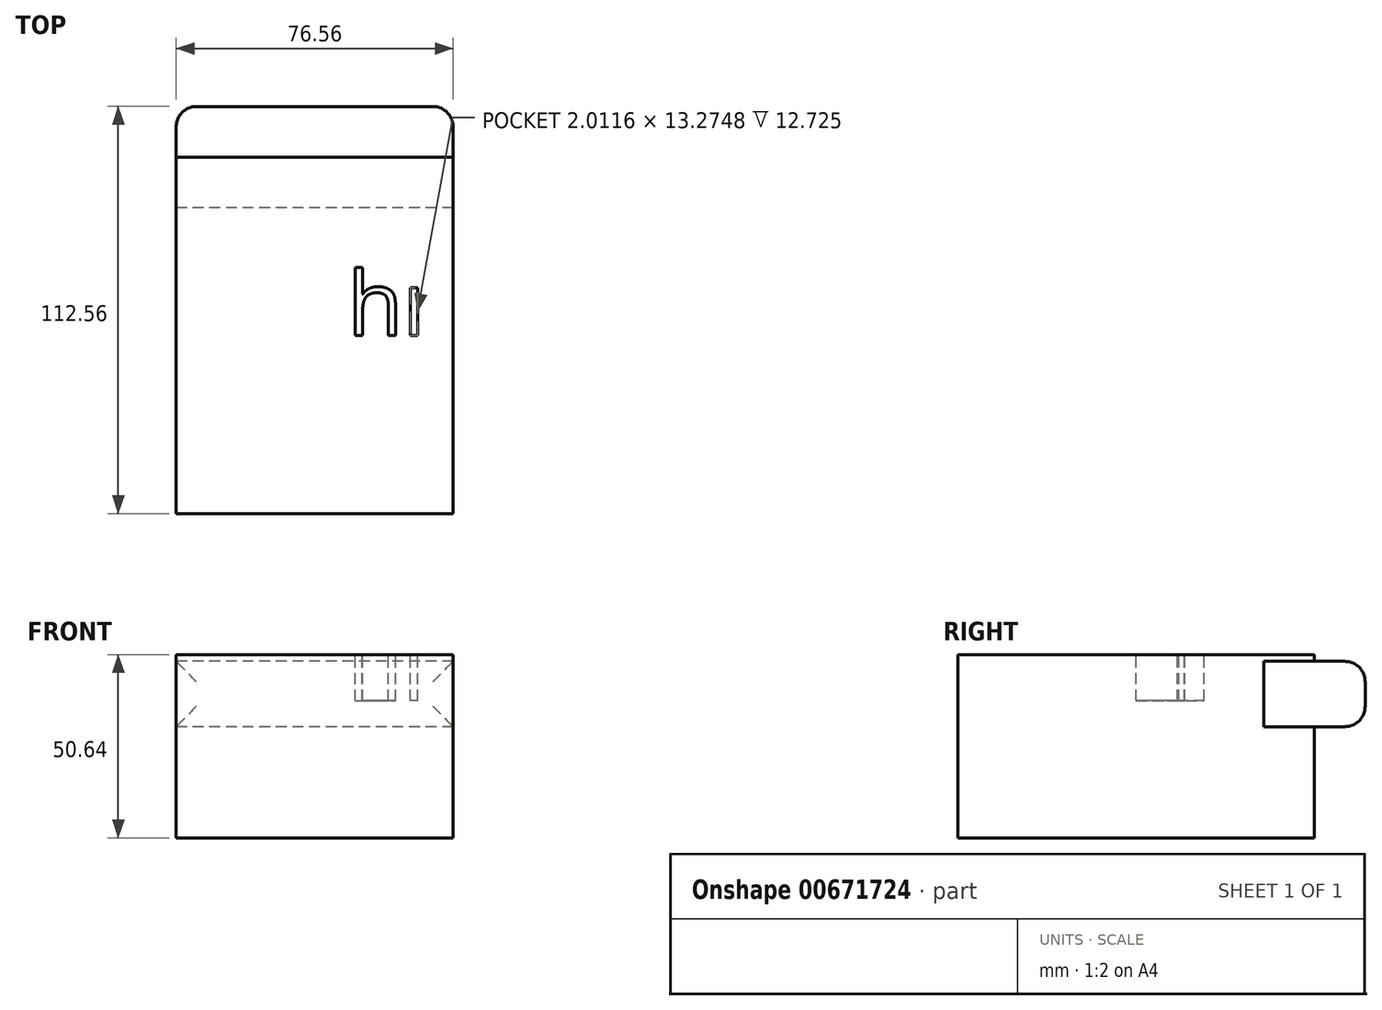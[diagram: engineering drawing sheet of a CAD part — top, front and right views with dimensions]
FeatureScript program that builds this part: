
annotation { "Feature Type Name" : "Feature", "Feature Type Description" : "" }
export const myFeature = defineFeature(function(context is Context, id is Id, definition is map)
    precondition{}
    {
        {
            var Q0;
            Q0=qCreatedBy(makeId("Right.planeOp"),FACE);
            var sketch = newSketch(context, id + "F0", { "sketchPlane" : qUnion([Q0])});
            skLineSegment(sketch, "E0.bottom", {"start": v(70.99, 0) * mm, "end": v(-27.58, 0) * mm});
            skLineSegment(sketch, "E0.top", {"start": v(70.99, 50.64) * mm, "end": v(-27.58, 50.64) * mm});
            skLineSegment(sketch, "E0.left", {"start": v(70.99, 0) * mm, "end": v(70.99, 50.64) * mm});
            skLineSegment(sketch, "E0.right", {"start": v(-27.58, 0) * mm, "end": v(-27.58, 50.64) * mm});
            skPoint(sketch, "E0.middle", {"position": v(21.7, 25.32) * mm});
            skLineSegment(sketch, "E1.bottom", {"start": v(84.98, 48.8) * mm, "end": v(57, 48.8) * mm});
            skLineSegment(sketch, "E1.top", {"start": v(84.98, 30.74) * mm, "end": v(57, 30.74) * mm});
            skLineSegment(sketch, "E1.left", {"start": v(84.98, 48.8) * mm, "end": v(84.98, 30.74) * mm});
            skLineSegment(sketch, "E1.right", {"start": v(57, 48.8) * mm, "end": v(57, 30.74) * mm});
            skPoint(sketch, "E1.middle", {"position": v(70.99, 39.77) * mm});
            skSolve(sketch);
        }
        {
            var Q0;
            {var subQ4=sQuery(id+"F0.wireOp",EDGE,"E0.bottom");Q0=makeQuery(id+"F0.imprint","IMPRINT",FACE,{"disambiguationData":[TD([[makeQuery(id+"F0.imprint","IMPRINT",EDGE,{"derivedFrom":subQ4}),-1.0]])]});}
            var sketch = newSketch(context, id + "F1", { "sketchPlane" : qUnion([Q0])});
            skSolve(sketch);
        }
        {
            var Q0;
            {var subQ4=sQuery(id+"F0.wireOp",EDGE,"E0.bottom");Q0=makeQuery(id+"F1.imprint","IMPRINT",FACE,{"disambiguationData":[TD([[makeQuery(id+"F1.imprint","IMPRINT",EDGE,{"derivedFrom":makeQuery(id+"F0.imprint","IMPRINT",EDGE,{"derivedFrom":subQ4})}),-1.0]])]});}
            var Q1;
            {var subQ5=sQuery(id+"F0.wireOp",EDGE,"E1.left");Q1=makeQuery(id+"F0.imprint","IMPRINT",FACE,{"disambiguationData":[TD([[makeQuery(id+"F0.imprint","IMPRINT",EDGE,{"derivedFrom":subQ5}),-1.0]])]});}
            var Q2;
            {var subQ5=sQuery(id+"F0.wireOp",EDGE,"E1.right");Q2=makeQuery(id+"F0.imprint","IMPRINT",FACE,{"disambiguationData":[TD([[makeQuery(id+"F0.imprint","IMPRINT",EDGE,{"derivedFrom":subQ5}),1.0]])]});}
            extrude(context, id + "F2", {"entities" : qUnion([Q0, Q1, Q2]), "depth" : 76.56 * mm, "offsetDistance" : 25.4 * mm});
        }
        {
            var Q0;
            Q0=makeQuery(id+"F2.opExtrude","SWEPT_EDGE",EDGE,{"disambiguationData":[OSD([sQuery(id+"F0.wireOp",EDGE,"E1.top"),sQuery(id+"F0.wireOp",EDGE,"E1.left")])]});
            var Q1;
            Q1=makeQuery(id+"F2.opExtrude","SWEPT_EDGE",EDGE,{"disambiguationData":[OSD([sQuery(id+"F0.wireOp",EDGE,"E1.bottom"),sQuery(id+"F0.wireOp",EDGE,"E1.left")])]});
            var Q2;
            Q2=makeQuery(id+"F2.opExtrude","CAP_EDGE",EDGE,{"disambiguationData":[OSD([sQuery(id+"F0.wireOp",EDGE,"E1.left")])],"isStart":false});
            var Q3;
            Q3=makeQuery(id+"F2.opExtrude","CAP_EDGE",EDGE,{"disambiguationData":[OSD([sQuery(id+"F0.wireOp",EDGE,"E1.left")])],"isStart":true});
            fillet(context, id + "F3", {"entities" : qUnion([Q0, Q1, Q2, Q3]), "radius" : 5.6 * mm, "tangentPropagation" : true, "allowEdgeOverflow" : false});
        }
        {
            var Q0;
            Q0=makeQuery(id+"F2.opExtrude","SWEPT_FACE",FACE,{"disambiguationData":[OSD([sQuery(id+"F0.wireOp",EDGE,"E0.top")])]});
            var sketch = newSketch(context, id + "F4", { "sketchPlane" : qUnion([Q0])});
            skText(sketch, "E2", { "text": "hi", "fontName": "OpenSans-Regular.ttf"});
            const initialGuessF4  = {"E2": [0.0474, 0.02166, 1, 0, 0.01786]};
            skSetInitialGuess(sketch, initialGuessF4);
            skSolve(sketch);
        }
        {
            var Q0;
            Q0=makeQuery(id+"F4.imprint","IMPRINT",FACE,{"disambiguationData":[TD([[makeQuery(id+"F4.imprint","IMPRINT",EDGE,{"derivedFrom":sQuery(id+"F4.wireOp",EDGE,"E2.sketch_text.stroke-0")}),-1.0]])]});
            var Q1;
            Q1=makeQuery(id+"F4.imprint","IMPRINT",FACE,{"disambiguationData":[TD([[makeQuery(id+"F4.imprint","IMPRINT",EDGE,{"derivedFrom":sQuery(id+"F4.wireOp",EDGE,"E2.sketch_text.stroke-18")}),-1.0]])]});
            extrude(context, id + "F5", {"entities" : qUnion([Q0, Q1]), "operationType" : NewBodyOperationType.REMOVE, "oppositeDirection" : true, "depth" : 12.73 * mm, "offsetDistance" : 25.4 * mm});
        }
    });
